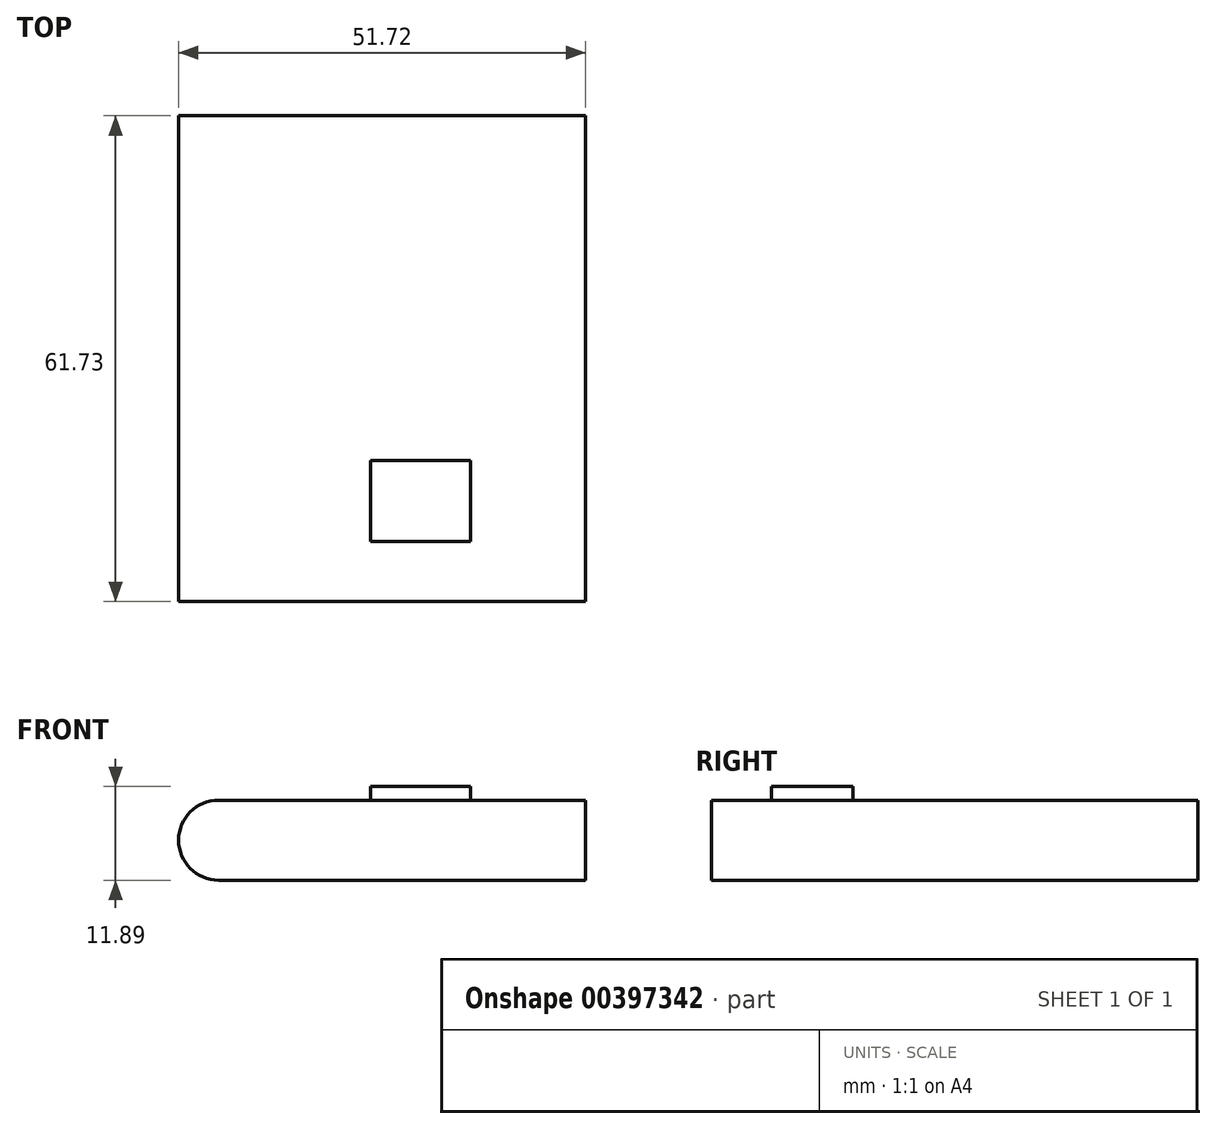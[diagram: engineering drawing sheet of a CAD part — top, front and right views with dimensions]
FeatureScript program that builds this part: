
annotation { "Feature Type Name" : "Feature", "Feature Type Description" : "" }
export const myFeature = defineFeature(function(context is Context, id is Id, definition is map)
    precondition{}
    {
        {
            var Q0;
            Q0=qCreatedBy(makeId("Top.planeOp"),FACE);
            var sketch = newSketch(context, id + "F0", { "sketchPlane" : qUnion([Q0])});
            skLineSegment(sketch, "E0.bottom", {"start": v(0, 0) * mm, "end": v(51.72, 0) * mm});
            skLineSegment(sketch, "E0.top", {"start": v(0, 32.6) * mm, "end": v(51.72, 32.6) * mm});
            skLineSegment(sketch, "E0.left", {"start": v(0, 0) * mm, "end": v(0, 32.6) * mm});
            skLineSegment(sketch, "E0.right", {"start": v(51.72, 0) * mm, "end": v(51.72, 32.6) * mm});
            skSolve(sketch);
        }
        {
            var Q0;
            Q0=makeQuery(id+"F0.imprint","IMPRINT",FACE,{"disambiguationData":[TD([[makeQuery(id+"F0.imprint","IMPRINT",EDGE,{"derivedFrom":sQuery(id+"F0.wireOp",EDGE,"E0.bottom")}),1.0]])]});
            extrude(context, id + "F1", {"entities" : qUnion([Q0]), "depth" : 10.16 * mm});
        }
        {
            var Q0;
            Q0=makeQuery(id+"F1.opExtrude","SWEPT_FACE",FACE,{"disambiguationData":[OSD([sQuery(id+"F0.wireOp",EDGE,"E0.bottom")])]});
            extrude(context, id + "F2", {"entities" : qUnion([Q0]), "operationType" : NewBodyOperationType.ADD, "depth" : 15.5 * mm});
        }
        {
            var Q0;
            {var subQ0=sQuery(id+"F0.wireOp",EDGE,"E0.bottom");Q0=makeQuery(id+"F2.boolean.opBoolean","MERGE",FACE,{"derivedFrom":[makeQuery(id+"F1.opExtrude","CAP_FACE",FACE,{"disambiguationData":[OSD([subQ0,sQuery(id+"F0.wireOp",EDGE,"E0.top"),sQuery(id+"F0.wireOp",EDGE,"E0.left"),sQuery(id+"F0.wireOp",EDGE,"E0.right")])],"isStart":false}),makeQuery(id+"F2.opExtrude","SWEPT_FACE",FACE,{"disambiguationData":[OSD([subQ0]),TDD([makeQuery(id+"F1.opExtrude","CAP_EDGE",EDGE,{"disambiguationData":[OSD([subQ0])],"isStart":false})])]})]});}
            var sketch = newSketch(context, id + "F3", { "sketchPlane" : qUnion([Q0])});
            skText(sketch, "E1", { "text": "BOOK\n", "fontName": "OpenSans-Regular.ttf"});
            const initialGuessF3  = {"E1": [0.00954, 0.02266, 1, 0, 0.00763]};
            skSetInitialGuess(sketch, initialGuessF3);
            skSolve(sketch);
        }
        {
            var Q0;
            {var subQ0=sQuery(id+"F0.wireOp",EDGE,"E0.left");var subQ1=sQuery(id+"F0.wireOp",EDGE,"E0.bottom");Q0=makeQuery(id+"F2.boolean.opBoolean","MERGE",EDGE,{"derivedFrom":[makeQuery(id+"F1.opExtrude","CAP_EDGE",EDGE,{"disambiguationData":[OSD([subQ0])],"isStart":false}),makeQuery(id+"F2.opExtrude","SWEPT_EDGE",EDGE,{"disambiguationData":[OSD([subQ1,subQ0]),TDD([makeQuery(id+"F1.opExtrude","CAP_VERTEX",VERTEX,{"disambiguationData":[OSD([subQ1,subQ0])],"isStart":false})])]})]});}
            fillet(context, id + "F4", {"entities" : qUnion([Q0]), "radius" : 5.08 * mm, "tangentPropagation" : true, "allowEdgeOverflow" : false});
        }
        {
            var Q0;
            {var subQ0=sQuery(id+"F0.wireOp",EDGE,"E0.left");var subQ1=sQuery(id+"F0.wireOp",EDGE,"E0.bottom");Q0=makeQuery(id+"F2.boolean.opBoolean","MERGE",EDGE,{"derivedFrom":[makeQuery(id+"F1.opExtrude","CAP_EDGE",EDGE,{"disambiguationData":[OSD([subQ0])],"isStart":true}),makeQuery(id+"F2.opExtrude","SWEPT_EDGE",EDGE,{"disambiguationData":[OSD([subQ1,subQ0]),TDD([makeQuery(id+"F1.opExtrude","CAP_VERTEX",VERTEX,{"disambiguationData":[OSD([subQ1,subQ0])],"isStart":true})])]})]});}
            fillet(context, id + "F5", {"entities" : qUnion([Q0]), "radius" : 5.08 * mm, "tangentPropagation" : true, "allowEdgeOverflow" : false});
        }
        {
            var Q0;
            Q0=makeQuery(id+"F2.opExtrude","CAP_FACE",FACE,{"disambiguationData":[OSD([sQuery(id+"F0.wireOp",EDGE,"E0.bottom")])],"isStart":false});
            extrude(context, id + "F6", {"entities" : qUnion([Q0]), "operationType" : NewBodyOperationType.ADD, "depth" : 13.64 * mm});
        }
        {
            var Q0;
            {var subQ0=sQuery(id+"F0.wireOp",EDGE,"E0.bottom");var subQ1=makeQuery(id+"F1.opExtrude","CAP_EDGE",EDGE,{"disambiguationData":[OSD([subQ0])],"isStart":false});Q0=makeQuery(id+"F6.boolean.opBoolean","MERGE",FACE,{"derivedFrom":[makeQuery(id+"F2.boolean.opBoolean","MERGE",FACE,{"derivedFrom":[makeQuery(id+"F1.opExtrude","CAP_FACE",FACE,{"disambiguationData":[OSD([subQ0,sQuery(id+"F0.wireOp",EDGE,"E0.top"),sQuery(id+"F0.wireOp",EDGE,"E0.left"),sQuery(id+"F0.wireOp",EDGE,"E0.right")])],"isStart":false}),makeQuery(id+"F2.opExtrude","SWEPT_FACE",FACE,{"disambiguationData":[OSD([subQ0]),TDD([subQ1])]})]}),makeQuery(id+"F6.opExtrude","SWEPT_FACE",FACE,{"disambiguationData":[OSD([subQ0]),TDD([makeQuery(id+"F2.opExtrude","CAP_EDGE",EDGE,{"disambiguationData":[OSD([subQ0]),TDD([subQ1])],"isStart":false})])]})]});}
            var sketch = newSketch(context, id + "F7", { "sketchPlane" : qUnion([Q0])});
            skLineSegment(sketch, "E2.bottom", {"start": v(24.38, -11.2) * mm, "end": v(37.1, -11.2) * mm});
            skLineSegment(sketch, "E2.top", {"start": v(24.38, -21.52) * mm, "end": v(37.1, -21.52) * mm});
            skLineSegment(sketch, "E2.left", {"start": v(24.38, -11.2) * mm, "end": v(24.38, -21.52) * mm});
            skLineSegment(sketch, "E2.right", {"start": v(37.1, -11.2) * mm, "end": v(37.1, -21.52) * mm});
            skSolve(sketch);
        }
        {
            var Q0;
            Q0 = qSketchRegion(id + "F7", true);
            extrude(context, id + "F8", {"entities" : qUnion([Q0]), "operationType" : NewBodyOperationType.ADD, "depth" : 1.73 * mm});
        }
    });
